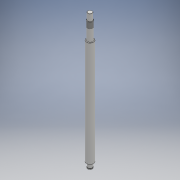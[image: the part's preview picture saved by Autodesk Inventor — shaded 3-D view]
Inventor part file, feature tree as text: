
AUTODESK INVENTOR PART (.ipt)
format: ipt  version: 2018 (Build 220112000, 112)  size: 126,976 bytes
history: native  units: mm
features: extrude x6, sketch x6, other x1, thread x1, chamfer x1
ambient origin geometry x8: Origin, YZ Plane, XZ Plane, XY Plane, X Axis, Y Axis, Z Axis, Center Point
bodies: Body1 (feature_tree)
feature tree (15):
  other  "Sólido1"
  extrude  "Extrusão1"  Depth=235.0mm TaperAngle=0.0deg
  extrude  "Extrusão2"  Depth=39.0mm TaperAngle=0.0deg
  extrude  "Extrusão3"  Depth=15.0mm TaperAngle=0.0deg
  extrude  "Extrusão4"  Depth=9.15mm TaperAngle=0.0deg
  extrude  "Extrusão5"  Depth=1.15mm TaperAngle=0.0deg
  extrude  "Extrusão6"  Depth=1.85mm TaperAngle=0.0deg
  thread  "Rosca1"  [1 undecoded]
  chamfer  "Chanfro1"  Distance=0.5mm Angle=45.0deg
  sketch  "Esboço1"  dims[d0=16.0mm d1=235.0mm d2=0.0mm]
  sketch  "Esboço2"  dims[d3=12.0mm d4=39.0mm d5=0.0mm]
  sketch  "Esboço3"  dims[d6=10.0mm d7=15.0mm d8=0.0mm]
  sketch  "Esboço4"  dims[d9=10.0mm d10=9.15mm d11=0.0mm]
  sketch  "Esboço5"  dims[d12=9.0mm d13=1.15mm d14=0.0mm]
  sketch  "Esboço6"  dims[d15=10.0mm d16=1.85mm d17=0.0mm d18=14.0mm d19=0.0mm d20=0.5mm d21=2.0mm d22=45.0deg]
note: 1 required parameter value undecoded (feature->parameter linkage not recoverable at this tier; creation-order binding heuristic only, values carry confidence <= 0.55)
